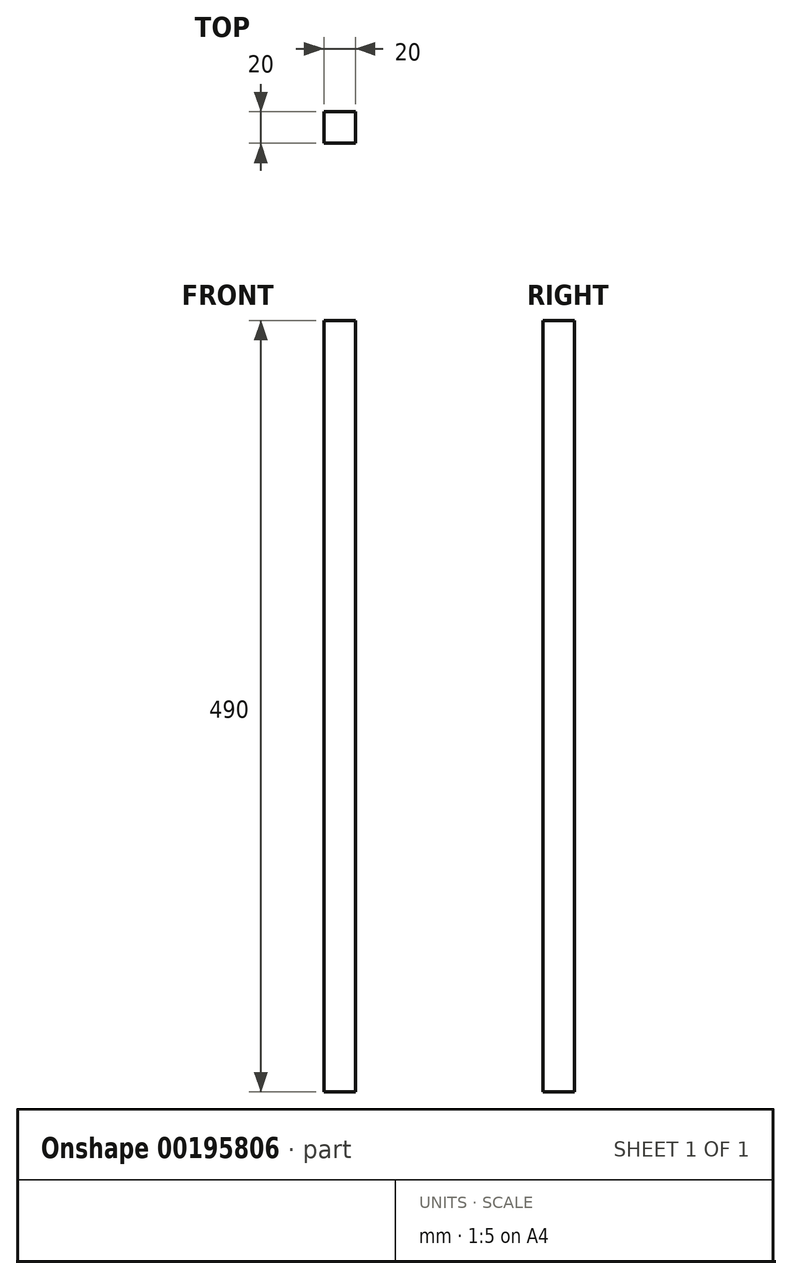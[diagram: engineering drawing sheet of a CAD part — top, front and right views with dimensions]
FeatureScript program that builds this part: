
annotation { "Feature Type Name" : "Feature", "Feature Type Description" : "" }
export const myFeature = defineFeature(function(context is Context, id is Id, definition is map)
    precondition{}
    {
        {
            var Q0;
            Q0=qCreatedBy(makeId("Top.planeOp"),FACE);
            var sketch = newSketch(context, id + "F0", { "sketchPlane" : qUnion([Q0])});
            skLineSegment(sketch, "E0.bottom", {"start": v(-91.8, -27.19) * mm, "end": v(-71.8, -27.19) * mm});
            skLineSegment(sketch, "E0.top", {"start": v(-91.8, -7.19) * mm, "end": v(-71.8, -7.19) * mm});
            skLineSegment(sketch, "E0.left", {"start": v(-91.8, -27.19) * mm, "end": v(-91.8, -7.19) * mm});
            skLineSegment(sketch, "E0.right", {"start": v(-71.8, -27.19) * mm, "end": v(-71.8, -7.19) * mm});
            skSolve(sketch);
        }
        {
            var Q0;
            Q0=makeQuery(id+"F0.imprint","IMPRINT",FACE,{"disambiguationData":[TD([[makeQuery(id+"F0.imprint","IMPRINT",EDGE,{"derivedFrom":sQuery(id+"F0.wireOp",EDGE,"E0.bottom")}),1.0]])]});
            extrude(context, id + "F1", {"entities" : qUnion([Q0]), "depth" : 490 * mm});
        }
    });
